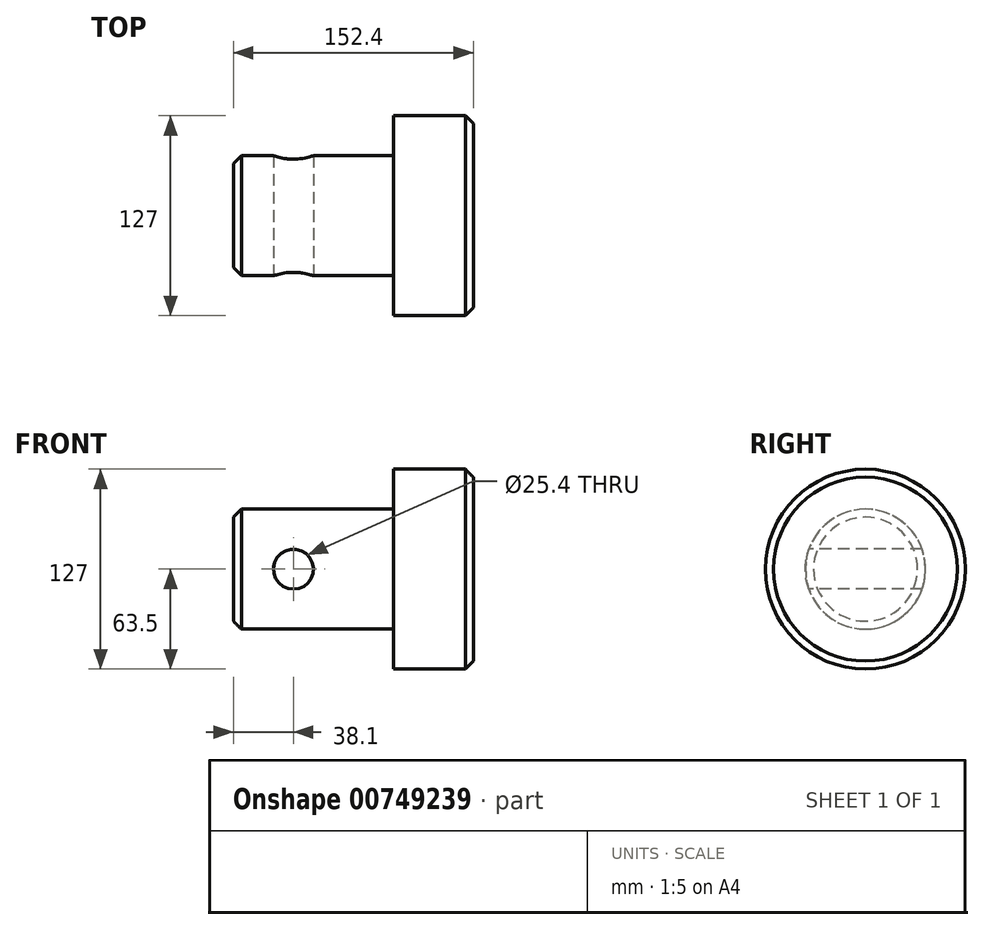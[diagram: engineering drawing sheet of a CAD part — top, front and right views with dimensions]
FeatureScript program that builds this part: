
annotation { "Feature Type Name" : "Feature", "Feature Type Description" : "" }
export const myFeature = defineFeature(function(context is Context, id is Id, definition is map)
    precondition{}
    {
        {
            var Q0;
            Q0=qCreatedBy(makeId("Front.planeOp"),FACE);
            var sketch = newSketch(context, id + "F0", { "sketchPlane" : qUnion([Q0])});
            skLineSegment(sketch, "E0", {"start": v(-101.6, 0) * mm, "end": v(50.8, 0) * mm});
            skLineSegment(sketch, "E1", {"start": v(50.8, 0) * mm, "end": v(50.8, -63.5) * mm});
            skLineSegment(sketch, "E2", {"start": v(50.8, -63.5) * mm, "end": v(0, -63.5) * mm});
            skLineSegment(sketch, "E3", {"start": v(0, -63.5) * mm, "end": v(0, -38.1) * mm});
            skLineSegment(sketch, "E4", {"start": v(0, -38.1) * mm, "end": v(-101.6, -38.1) * mm});
            skLineSegment(sketch, "E5", {"start": v(-101.6, -38.1) * mm, "end": v(-101.6, 0) * mm});
            skSolve(sketch);
        }
        {
            var Q0;
            Q0=makeQuery(id+"F0.imprint","IMPRINT",FACE,{"disambiguationData":[TD([[makeQuery(id+"F0.imprint","IMPRINT",EDGE,{"derivedFrom":sQuery(id+"F0.wireOp",EDGE,"E0")}),-1.0]])]});
            var Q1;
            Q1=sQuery(id+"F0.wireOp",EDGE,"E0");
            revolve(context, id + "F1", {"surfaceOperationType" : NewSurfaceOperationType.NEW, "entities" : qUnion([Q0]), "axis" : qUnion([Q1]), "revolveType" : RevolveType.FULL});
        }
        {
            var Q0;
            Q0=qCreatedBy(makeId("Front.planeOp"),FACE);
            cPlane(context, id + "F2", {"entities" : qUnion([Q0]), "cplaneType" : CPlaneType.OFFSET, "offset" : 38.1 * mm, "width" : 152.4 * mm, "height" : 152.4 * mm});
        }
        {
            var Q0;
            Q0=qCreatedBy(id+"F2.planeOp",FACE);
            var sketch = newSketch(context, id + "F3", { "sketchPlane" : qUnion([Q0])});
            skCircle(sketch, "E6", {"center": v(-63.5, 0) * mm, "radius": 12.7 * mm});
            skSolve(sketch);
        }
        {
            var Q0;
            Q0=sQuery(id+"F3.wireOp",VERTEX,"E6.center");
            var Q1;
            Q1=makeQuery(id+"F1.opRevolve","SWEPT_BODY",BODY,{"disambiguationData":[OSD([sQuery(id+"F0.wireOp",EDGE,"E0"),sQuery(id+"F0.wireOp",EDGE,"E1"),sQuery(id+"F0.wireOp",EDGE,"E2"),sQuery(id+"F0.wireOp",EDGE,"E3"),sQuery(id+"F0.wireOp",EDGE,"E4"),sQuery(id+"F0.wireOp",EDGE,"E5")])]});
            hole(context, id + "F4", {"style" : HoleStyle.SIMPLE, "endStyle" : HoleEndStyle.THROUGH, "holeDiameter" : 25.4 * mm, "majorDiameter" : 6.35 * mm, "isTappedThrough" : true, "tappedDepth" : 12.7 * mm, "tapClearance" : 3, "locations" : qUnion([Q0]), "scope" : qUnion([Q1])});
        }
        {
            var Q0;
            Q0=makeQuery(id+"F1.opRevolve","SWEPT_EDGE",EDGE,{"disambiguationData":[OSD([sQuery(id+"F0.wireOp",EDGE,"E1"),sQuery(id+"F0.wireOp",EDGE,"E2")])]});
            var Q1;
            Q1=makeQuery(id+"F1.opRevolve","SWEPT_EDGE",EDGE,{"disambiguationData":[OSD([sQuery(id+"F0.wireOp",EDGE,"E4"),sQuery(id+"F0.wireOp",EDGE,"E5")])]});
            chamfer(context, id + "F5", {"entities" : qUnion([Q0, Q1]), "width" : 5.08 * mm, "tangentPropagation" : true});
        }
    });
